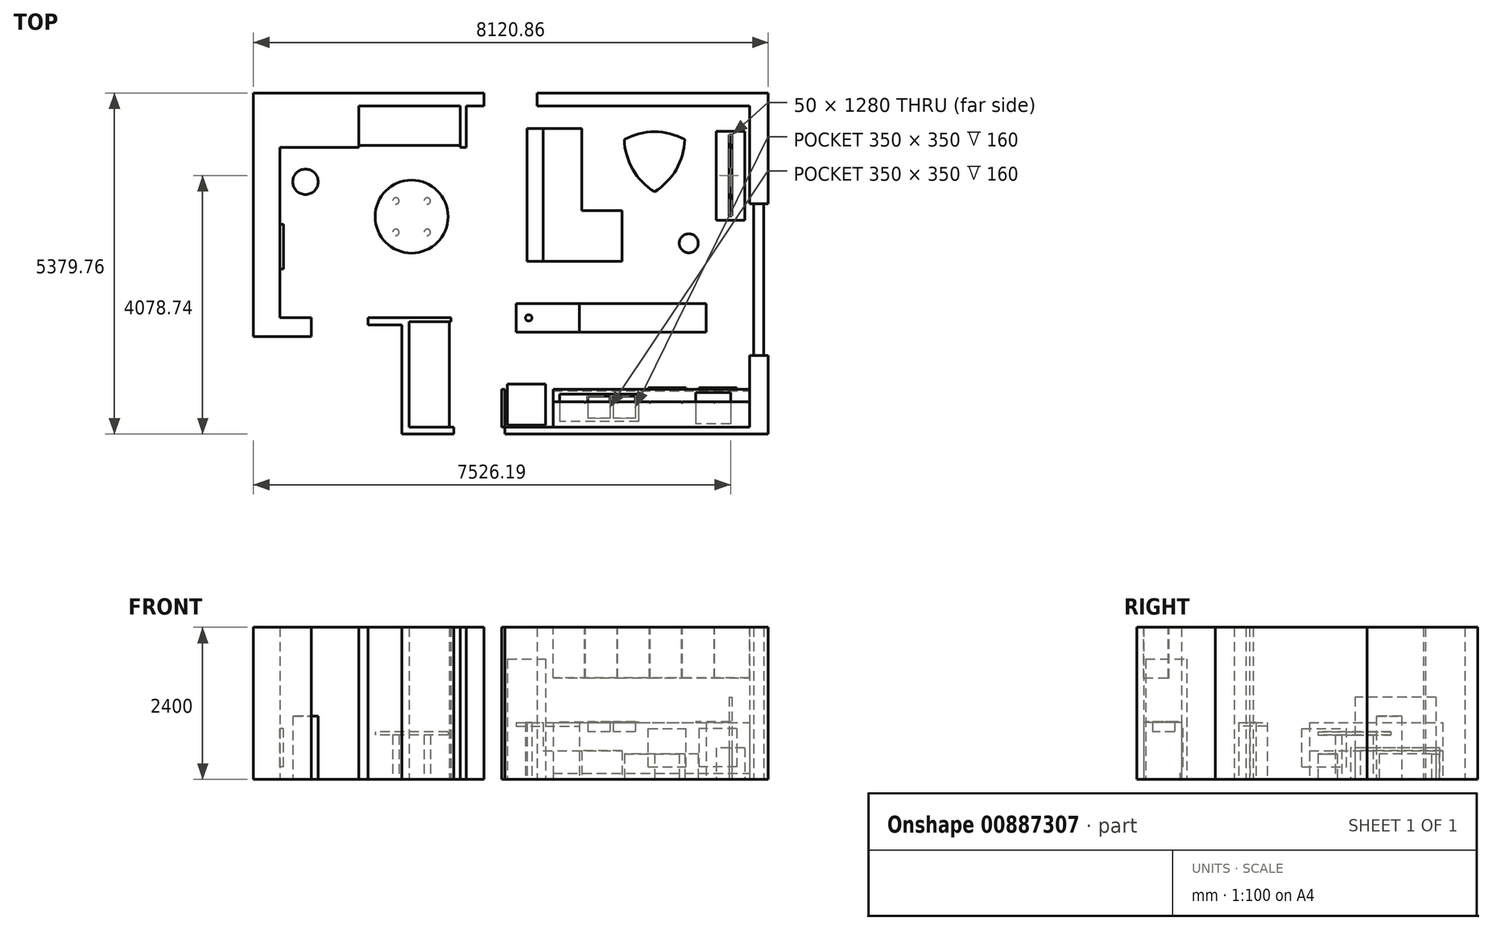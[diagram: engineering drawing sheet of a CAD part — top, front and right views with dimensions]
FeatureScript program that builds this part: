
annotation { "Feature Type Name" : "Feature", "Feature Type Description" : "" }
export const myFeature = defineFeature(function(context is Context, id is Id, definition is map)
    precondition{}
    {
        {
            var Q0;
            Q0=qCreatedBy(makeId("Top.planeOp"),FACE);
            var sketch = newSketch(context, id + "F0", { "sketchPlane" : qUnion([Q0])});
            skLineSegment(sketch, "E0", {"start": v(5332.87, -822.17) * mm, "end": v(1474.75, -822.17) * mm});
            skLineSegment(sketch, "E1", {"start": v(1474.75, -822.17) * mm, "end": v(1474.75, -222.17) * mm});
            skLineSegment(sketch, "E2", {"start": v(1474.75, -222.17) * mm, "end": v(1421.4, -222.17) * mm});
            skLineSegment(sketch, "E3", {"start": v(1421.4, -222.17) * mm, "end": v(1421.4, -822.17) * mm});
            skLineSegment(sketch, "E4", {"start": v(1421.4, -822.17) * mm, "end": v(1474.75, -822.17) * mm});
            skLineSegment(sketch, "E5", {"start": v(5332.87, 309.99) * mm, "end": v(5394.44, 309.99) * mm});
            skLineSegment(sketch, "E6", {"start": v(5394.44, 309.99) * mm, "end": v(5394.44, 2704.75) * mm});
            skLineSegment(sketch, "E7", {"start": v(5394.44, 2704.75) * mm, "end": v(5332.87, 2704.75) * mm});
            skLineSegment(sketch, "E8", {"start": v(5332.87, 2704.75) * mm, "end": v(5332.87, 4243.63) * mm});
            skLineSegment(sketch, "E9", {"start": v(5332.87, 4243.63) * mm, "end": v(1981.19, 4243.63) * mm});
            skLineSegment(sketch, "E10", {"start": v(1981.19, 4243.63) * mm, "end": v(1981.19, 4451) * mm});
            skLineSegment(sketch, "E11", {"start": v(1981.19, 4451) * mm, "end": v(5626.54, 4451) * mm});
            skLineSegment(sketch, "E12", {"start": v(5626.54, 4451) * mm, "end": v(5626.54, 2704.75) * mm});
            skLineSegment(sketch, "E13", {"start": v(5626.54, 2704.75) * mm, "end": v(5394.44, 2704.75) * mm});
            skLineSegment(sketch, "E14", {"start": v(5394.44, 309.99) * mm, "end": v(5626.54, 309.99) * mm});
            skPoint(sketch, "E14.endSnap0", {"position": v(5363.66, 309.99) * mm});
            skLineSegment(sketch, "E15", {"start": v(5626.54, 309.99) * mm, "end": v(5626.54, -928.77) * mm});
            skLineSegment(sketch, "E16", {"start": v(5626.54, -928.77) * mm, "end": v(1474.75, -928.77) * mm});
            skLineSegment(sketch, "E17", {"start": v(1474.75, -928.77) * mm, "end": v(1474.75, -822.17) * mm});
            skLineSegment(sketch, "E18", {"start": v(5558.56, 2704.75) * mm, "end": v(5558.56, 309.99) * mm});
            skLineSegment(sketch, "E19", {"start": v(-37.13, -822.17) * mm, "end": v(664.8, -822.17) * mm});
            skLineSegment(sketch, "E20", {"start": v(664.8, -822.17) * mm, "end": v(664.8, -928.77) * mm});
            skLineSegment(sketch, "E21", {"start": v(664.8, -928.77) * mm, "end": v(-150.57, -928.77) * mm});
            skLineSegment(sketch, "E22", {"start": v(-150.57, -928.77) * mm, "end": v(-150.57, 905.53) * mm});
            skLineSegment(sketch, "E23", {"start": v(-150.57, 905.53) * mm, "end": v(-37.13, 905.53) * mm});
            skLineSegment(sketch, "E24", {"start": v(-37.13, 905.53) * mm, "end": v(-37.13, -26.35) * mm});
            skLineSegment(sketch, "E25", {"start": v(5332.87, 309.99) * mm, "end": v(5332.87, -822.17) * mm});
            skLineSegment(sketch, "E26", {"start": v(-37.13, 905.53) * mm, "end": v(-37.13, -822.17) * mm});
            skLineSegment(sketch, "E27.bottom", {"start": v(1511.94, -792.17) * mm, "end": v(2111.94, -792.17) * mm});
            skLineSegment(sketch, "E27.left", {"start": v(1511.94, -792.17) * mm, "end": v(1511.94, -142.17) * mm});
            skLineSegment(sketch, "E28", {"start": v(1511.94, -142.17) * mm, "end": v(2111.94, -142.17) * mm});
            skLineSegment(sketch, "E29", {"start": v(2111.94, -142.17) * mm, "end": v(2111.94, -792.17) * mm});
            skLineSegment(sketch, "E30", {"start": v(5332.87, -822.17) * mm, "end": v(2232.87, -822.17) * mm, "construction": true});
            skLineSegment(sketch, "E31", {"start": v(2232.87, -822.17) * mm, "end": v(2232.87, -222.17) * mm});
            skLineSegment(sketch, "E32", {"start": v(5332.87, 309.99) * mm, "end": v(4732.87, 309.99) * mm, "construction": true});
            skLineSegment(sketch, "E33", {"start": v(2232.87, -222.17) * mm, "end": v(4732.87, -222.17) * mm});
            skLineSegment(sketch, "E34", {"start": v(4732.87, -222.17) * mm, "end": v(4732.87, 309.99) * mm, "construction": true});
            skLineSegment(sketch, "E35", {"start": v(1647.48, 677.83) * mm, "end": v(4647.48, 677.83) * mm});
            skLineSegment(sketch, "E36", {"start": v(4647.48, 677.83) * mm, "end": v(4647.48, 1127.83) * mm});
            skLineSegment(sketch, "E37", {"start": v(4647.48, 1127.83) * mm, "end": v(1647.48, 1127.83) * mm});
            skLineSegment(sketch, "E38", {"start": v(1647.48, 1127.83) * mm, "end": v(1647.48, 677.83) * mm, "construction": true});
            skLineSegment(sketch, "E39", {"start": v(1822.87, 1793.63) * mm, "end": v(1822.87, 3893.63) * mm});
            skLineSegment(sketch, "E40", {"start": v(1822.87, 3893.63) * mm, "end": v(2682.87, 3893.63) * mm});
            skLineSegment(sketch, "E41", {"start": v(2682.87, 3893.63) * mm, "end": v(2682.87, 2593.63) * mm});
            skLineSegment(sketch, "E42", {"start": v(1822.87, 1793.63) * mm, "end": v(3322.87, 1793.63) * mm});
            skLineSegment(sketch, "E43", {"start": v(3322.87, 1793.63) * mm, "end": v(3322.87, 2593.63) * mm});
            skLineSegment(sketch, "E44", {"start": v(3322.87, 2593.63) * mm, "end": v(2682.87, 2593.63) * mm});
            skLineSegment(sketch, "E45", {"start": v(2072.87, 1793.63) * mm, "end": v(2072.87, 3893.63) * mm});
            skLineSegment(sketch, "E46", {"start": v(2232.87, -549.5) * mm, "end": v(2332.87, -549.5) * mm, "construction": true});
            skLineSegment(sketch, "E47", {"start": v(2332.87, -302.17) * mm, "end": v(2332.87, -732.17) * mm});
            skLineSegment(sketch, "E48", {"start": v(2332.87, -302.17) * mm, "end": v(3582.87, -302.17) * mm});
            skLineSegment(sketch, "E49", {"start": v(3582.87, -302.17) * mm, "end": v(3582.87, -732.17) * mm});
            skLineSegment(sketch, "E50", {"start": v(3582.87, -732.17) * mm, "end": v(2332.87, -732.17) * mm});
            skLineSegment(sketch, "E51", {"start": v(3582.87, -517.17) * mm, "end": v(3532.87, -517.17) * mm, "construction": true});
            skLineSegment(sketch, "E52", {"start": v(3532.87, -517.17) * mm, "end": v(3182.87, -517.17) * mm, "construction": true});
            skLineSegment(sketch, "E53", {"start": v(3182.87, -517.17) * mm, "end": v(3132.87, -517.17) * mm, "construction": true});
            skLineSegment(sketch, "E54", {"start": v(3132.87, -517.17) * mm, "end": v(2782.87, -517.17) * mm, "construction": true});
            skLineSegment(sketch, "E55", {"start": v(3352.05, -302.17) * mm, "end": v(3352.05, -332.17) * mm, "construction": true});
            skLineSegment(sketch, "E56", {"start": v(3352.05, -332.17) * mm, "end": v(3352.05, -682.17) * mm, "construction": true});
            skLineSegment(sketch, "E57.bottom", {"start": v(3532.87, -332.17) * mm, "end": v(3182.87, -332.17) * mm});
            skLineSegment(sketch, "E57.top", {"start": v(3532.87, -682.17) * mm, "end": v(3182.87, -682.17) * mm});
            skLineSegment(sketch, "E57.left", {"start": v(3532.87, -332.17) * mm, "end": v(3532.87, -682.17) * mm});
            skLineSegment(sketch, "E57.right", {"start": v(3182.87, -332.17) * mm, "end": v(3182.87, -682.17) * mm});
            skLineSegment(sketch, "E58.bottom", {"start": v(3132.87, -332.17) * mm, "end": v(2782.87, -332.17) * mm});
            skLineSegment(sketch, "E58.top", {"start": v(3132.87, -682.17) * mm, "end": v(2782.87, -682.17) * mm});
            skLineSegment(sketch, "E58.left", {"start": v(3132.87, -332.17) * mm, "end": v(3132.87, -682.17) * mm});
            skLineSegment(sketch, "E58.right", {"start": v(2782.87, -332.17) * mm, "end": v(2782.87, -682.17) * mm});
            skLineSegment(sketch, "E59.bottom", {"start": v(5032.87, -272.17) * mm, "end": v(4482.87, -272.17) * mm});
            skLineSegment(sketch, "E59.top", {"start": v(5032.87, -772.17) * mm, "end": v(4482.87, -772.17) * mm});
            skLineSegment(sketch, "E59.left", {"start": v(5032.87, -272.17) * mm, "end": v(5032.87, -772.17) * mm});
            skLineSegment(sketch, "E59.right", {"start": v(4482.87, -272.17) * mm, "end": v(4482.87, -772.17) * mm});
            skLineSegment(sketch, "E60", {"start": v(1647.48, 677.83) * mm, "end": v(2647.48, 677.83) * mm, "construction": true});
            skLineSegment(sketch, "E61", {"start": v(2647.48, 677.83) * mm, "end": v(2647.48, 1127.83) * mm});
            skLineSegment(sketch, "E62", {"start": v(2647.48, 902.83) * mm, "end": v(1847.48, 902.83) * mm, "construction": true});
            skCircle(sketch, "E63", {"center": v(1847.48, 902.83) * mm, "radius": 50 * mm});
            skLineSegment(sketch, "E64", {"start": v(5626.54, 309.99) * mm, "end": v(5626.54, -6920.01) * mm, "construction": true});
            skLineSegment(sketch, "E65", {"start": v(5626.54, -6920.01) * mm, "end": v(109096.54, -6920.01) * mm, "construction": true});
            skLineSegment(sketch, "E66", {"start": v(-150.57, 905.53) * mm, "end": v(-687.76, 905.53) * mm});
            skLineSegment(sketch, "E67", {"start": v(-687.76, 905.53) * mm, "end": v(-687.76, 793.16) * mm});
            skLineSegment(sketch, "E68", {"start": v(-687.76, 793.16) * mm, "end": v(-150.57, 793.16) * mm});
            skLineSegment(sketch, "E69", {"start": v(1145.44, 4243.63) * mm, "end": v(-834.24, 4243.63) * mm});
            skLineSegment(sketch, "E70", {"start": v(-834.24, 4243.63) * mm, "end": v(-834.24, 3594.84) * mm});
            skLineSegment(sketch, "E71", {"start": v(-834.24, 3594.84) * mm, "end": v(-2078.37, 3594.84) * mm});
            skLineSegment(sketch, "E72", {"start": v(-2078.37, 3594.84) * mm, "end": v(-2078.37, 905.53) * mm});
            skLineSegment(sketch, "E73", {"start": v(-2078.37, 905.53) * mm, "end": v(-1579.23, 905.53) * mm});
            skLineSegment(sketch, "E74", {"start": v(-1579.23, 905.53) * mm, "end": v(-1579.23, 605.3) * mm});
            skLineSegment(sketch, "E75", {"start": v(-1579.23, 605.3) * mm, "end": v(-2494.32, 605.3) * mm});
            skLineSegment(sketch, "E76", {"start": v(-2494.32, 605.3) * mm, "end": v(-2494.32, 4451) * mm});
            skLineSegment(sketch, "E77", {"start": v(-2494.32, 4451) * mm, "end": v(1145.44, 4451) * mm});
            skLineSegment(sketch, "E78", {"start": v(1145.44, 4451) * mm, "end": v(1145.44, 4243.63) * mm});
            skLineSegment(sketch, "E79", {"start": v(5332.87, 4243.63) * mm, "end": v(5332.87, 4451) * mm});
            skCircle(sketch, "E80", {"center": v(0, 2500.55) * mm, "radius": 350 * mm, "construction": true});
            skLineSegment(sketch, "E81", {"start": v(-247.49, 2748.03) * mm, "end": v(247.49, 2748.03) * mm, "construction": true});
            skLineSegment(sketch, "E82", {"start": v(247.49, 2748.03) * mm, "end": v(247.49, 2253.06) * mm, "construction": true});
            skLineSegment(sketch, "E83", {"start": v(247.49, 2253.06) * mm, "end": v(-247.49, 2253.06) * mm, "construction": true});
            skCircle(sketch, "E84", {"center": v(-247.49, 2748.03) * mm, "radius": 50 * mm});
            skCircle(sketch, "E85", {"center": v(247.49, 2748.03) * mm, "radius": 50 * mm});
            skCircle(sketch, "E86", {"center": v(247.49, 2253.06) * mm, "radius": 50 * mm});
            skCircle(sketch, "E87", {"center": v(-247.49, 2253.06) * mm, "radius": 50 * mm});
            skCircle(sketch, "E88", {"center": v(0, 2500.55) * mm, "radius": 575 * mm});
            skCircle(sketch, "E89", {"center": v(3832.87, 3443.63) * mm, "radius": 550 * mm, "construction": true});
            skLineSegment(sketch, "E90", {"start": v(3832.87, 3443.63) * mm, "end": v(3832.87, 2893.63) * mm, "construction": true});
            skArc(sketch, "E91", {"start": v(3832.87, 2893.63) * mm, "mid": v(4175.58, 3245.77) * mm, "end": v(4309.19, 3718.63) * mm});
            skArc(sketch, "E92", {"start": v(4309.19, 3718.63) * mm, "mid": v(3832.87, 3839.36) * mm, "end": v(3356.56, 3718.63) * mm});
            skArc(sketch, "E93", {"start": v(3356.56, 3718.63) * mm, "mid": v(3490.17, 3245.77) * mm, "end": v(3832.87, 2893.63) * mm});
            skLineSegment(sketch, "E94", {"start": v(3832.87, 3443.63) * mm, "end": v(4309.19, 3718.63) * mm, "construction": true});
            skLineSegment(sketch, "E95", {"start": v(3832.87, 3443.63) * mm, "end": v(3356.56, 3718.63) * mm, "construction": true});
            skLineSegment(sketch, "E96", {"start": v(4309.19, 3718.63) * mm, "end": v(3356.56, 3718.63) * mm, "construction": true});
            skLineSegment(sketch, "E97", {"start": v(3356.56, 3718.63) * mm, "end": v(3832.87, 2893.63) * mm, "construction": true});
            skLineSegment(sketch, "E98", {"start": v(3832.87, 2893.63) * mm, "end": v(4309.19, 3718.63) * mm, "construction": true});
            skCircle(sketch, "E99", {"center": v(4373.05, 2080.44) * mm, "radius": 150 * mm});
            skLineSegment(sketch, "E100", {"start": v(4732.87, -222.17) * mm, "end": v(5332.87, -222.17) * mm});
            skLineSegment(sketch, "E101", {"start": v(865.76, 4243.63) * mm, "end": v(865.76, 3594.84) * mm});
            skLineSegment(sketch, "E102", {"start": v(865.76, 3594.84) * mm, "end": v(765.76, 3594.84) * mm});
            skLineSegment(sketch, "E103", {"start": v(765.76, 3594.84) * mm, "end": v(765.76, 4243.63) * mm});
            skLineSegment(sketch, "E104", {"start": v(765.76, 3627.05) * mm, "end": v(-834.24, 3627.05) * mm});
            skLineSegment(sketch, "E105", {"start": v(597.97, -822.17) * mm, "end": v(597.97, 845.53) * mm});
            skLineSegment(sketch, "E106", {"start": v(597.97, 905.53) * mm, "end": v(624.1, 905.53) * mm});
            skLineSegment(sketch, "E107", {"start": v(624.1, 905.53) * mm, "end": v(624.1, 845.53) * mm});
            skLineSegment(sketch, "E108", {"start": v(624.1, 845.53) * mm, "end": v(-37.13, 845.53) * mm});
            skLineSegment(sketch, "E109", {"start": v(-37.13, 905.53) * mm, "end": v(597.97, 905.53) * mm});
            skCircle(sketch, "E110", {"center": v(-1673.98, 3049.9) * mm, "radius": 200 * mm});
            skLineSegment(sketch, "E111.bottom", {"start": v(5257.71, 3843.63) * mm, "end": v(4807.71, 3843.63) * mm});
            skLineSegment(sketch, "E111.top", {"start": v(5257.71, 2443.63) * mm, "end": v(4807.71, 2443.63) * mm});
            skLineSegment(sketch, "E111.left", {"start": v(5257.71, 3843.63) * mm, "end": v(5257.71, 2443.63) * mm});
            skLineSegment(sketch, "E111.right", {"start": v(4807.71, 3843.63) * mm, "end": v(4807.71, 2443.63) * mm});
            skLineSegment(sketch, "E112.bottom", {"start": v(5006.87, 3789.97) * mm, "end": v(5056.87, 3789.97) * mm});
            skLineSegment(sketch, "E112.top", {"start": v(5006.87, 2509.97) * mm, "end": v(5056.87, 2509.97) * mm});
            skLineSegment(sketch, "E112.left", {"start": v(5006.87, 3789.97) * mm, "end": v(5006.87, 2509.97) * mm});
            skLineSegment(sketch, "E112.right", {"start": v(5056.87, 3789.97) * mm, "end": v(5056.87, 2509.97) * mm});
            skSolve(sketch);
        }
        {
            var Q0;
            {var subQ3=sQuery(id+"F0.wireOp",EDGE,"E7");Q0=makeQuery(id+"F0.imprint","IMPRINT",FACE,{"disambiguationData":[TD([[makeQuery(id+"F0.imprint","IMPRINT",EDGE,{"derivedFrom":subQ3}),-1.0]])]});}
            var Q1;
            {var subQ1=sQuery(id+"F0.wireOp",EDGE,"E5");Q1=makeQuery(id+"F0.imprint","IMPRINT",FACE,{"disambiguationData":[TD([[makeQuery(id+"F0.imprint","IMPRINT",EDGE,{"derivedFrom":subQ1}),-1.0]])]});}
            var Q2;
            {var subQ1=sQuery(id+"F0.wireOp",EDGE,"E20");Q2=makeQuery(id+"F0.imprint","IMPRINT",FACE,{"disambiguationData":[TD([[makeQuery(id+"F0.imprint","IMPRINT",EDGE,{"derivedFrom":subQ1}),-1.0]])]});}
            var Q3;
            Q3=makeQuery(id+"F0.imprint","IMPRINT",FACE,{"disambiguationData":[TD([[makeQuery(id+"F0.imprint","IMPRINT",EDGE,{"derivedFrom":sQuery(id+"F0.wireOp",EDGE,"E1")}),1.0]])]});
            var Q4;
            {var subQ0=sQuery(id+"F0.wireOp",EDGE,"E71");Q4=makeQuery(id+"F0.imprint","IMPRINT",FACE,{"disambiguationData":[TD([[makeQuery(id+"F0.imprint","IMPRINT",EDGE,{"derivedFrom":subQ0}),-1.0]])]});}
            var Q5;
            {var subQ0=sQuery(id+"F0.wireOp",EDGE,"E66");Q5=makeQuery(id+"F0.imprint","IMPRINT",FACE,{"disambiguationData":[TD([[makeQuery(id+"F0.imprint","IMPRINT",EDGE,{"derivedFrom":subQ0}),1.0]])]});}
            var Q6;
            Q6=makeQuery(id+"F0.imprint","IMPRINT",FACE,{"disambiguationData":[TD([[makeQuery(id+"F0.imprint","IMPRINT",EDGE,{"derivedFrom":sQuery(id+"F0.wireOp",EDGE,"E9")}),-1.0]])]});
            var Q7;
            {var subQ5=sQuery(id+"F0.wireOp",EDGE,"E101");Q7=makeQuery(id+"F0.imprint","IMPRINT",FACE,{"disambiguationData":[TD([[makeQuery(id+"F0.imprint","IMPRINT",EDGE,{"derivedFrom":subQ5}),-1.0]])]});}
            var Q8;
            Q8=makeQuery(id+"F0.imprint","IMPRINT",FACE,{"disambiguationData":[TD([[makeQuery(id+"F0.imprint","IMPRINT",EDGE,{"derivedFrom":sQuery(id+"F0.wireOp",EDGE,"E106")}),-1.0]])]});
            extrude(context, id + "F1", {"entities" : qUnion([Q0, Q1, Q2, Q3, Q4, Q5, Q6, Q7, Q8]), "depth" : 2400 * mm, "offsetDistance" : 25 * mm});
        }
        {
            var Q0;
            {var subQ4=sQuery(id+"F0.wireOp",EDGE,"E31");Q0=makeQuery(id+"F0.imprint","IMPRINT",FACE,{"disambiguationData":[TD([[makeQuery(id+"F0.imprint","IMPRINT",EDGE,{"derivedFrom":subQ4}),-1.0]])]});}
            var Q1;
            {var subQ2=sQuery(id+"F0.wireOp",EDGE,"E36");Q1=makeQuery(id+"F0.imprint","IMPRINT",FACE,{"disambiguationData":[TD([[makeQuery(id+"F0.imprint","IMPRINT",EDGE,{"derivedFrom":subQ2}),1.0]])]});}
            var Q2;
            Q2=makeQuery(id+"F0.imprint","IMPRINT",FACE,{"disambiguationData":[TD([[makeQuery(id+"F0.imprint","IMPRINT",EDGE,{"derivedFrom":sQuery(id+"F0.wireOp",EDGE,"E63")}),1.0]])]});
            extrude(context, id + "F2", {"entities" : qUnion([Q0, Q1, Q2]), "depth" : 900 * mm, "offsetDistance" : 25 * mm});
        }
        {
            var Q0;
            Q0=makeQuery(id+"F1.opExtrude","CAP_FACE",FACE,{"disambiguationData":[OSD([sQuery(id+"F0.wireOp",EDGE,"E0"),sQuery(id+"F0.wireOp",EDGE,"E5"),sQuery(id+"F0.wireOp",EDGE,"E14"),sQuery(id+"F0.wireOp",EDGE,"E15"),sQuery(id+"F0.wireOp",EDGE,"E16"),sQuery(id+"F0.wireOp",EDGE,"E17"),sQuery(id+"F0.wireOp",EDGE,"E25")])],"isStart":false});
            var sketch = newSketch(context, id + "F3", { "sketchPlane" : qUnion([Q0])});
            skLineSegment(sketch, "E113", {"start": v(5332.87, -822.17) * mm, "end": v(2232.87, -822.17) * mm});
            skLineSegment(sketch, "E114", {"start": v(2232.87, -822.17) * mm, "end": v(2232.87, -422.17) * mm});
            skLineSegment(sketch, "E115", {"start": v(2232.87, -422.17) * mm, "end": v(5332.87, -422.17) * mm});
            skLineSegment(sketch, "E116", {"start": v(5332.87, -422.17) * mm, "end": v(5332.87, -822.17) * mm});
            skSolve(sketch);
        }
        {
            var Q0;
            Q0=makeQuery(id+"F3.imprint","IMPRINT",FACE,{"disambiguationData":[TD([[makeQuery(id+"F3.imprint","IMPRINT",EDGE,{"derivedFrom":sQuery(id+"F3.wireOp",EDGE,"E113")}),-1.0]])]});
            extrude(context, id + "F4", {"entities" : qUnion([Q0]), "oppositeDirection" : true, "depth" : 800 * mm, "offsetDistance" : 25 * mm});
        }
        {
            var Q0;
            Q0=makeQuery(id+"F0.imprint","IMPRINT",FACE,{"disambiguationData":[TD([[makeQuery(id+"F0.imprint","IMPRINT",EDGE,{"derivedFrom":sQuery(id+"F0.wireOp",EDGE,"E27.bottom")}),1.0]])]});
            extrude(context, id + "F5", {"entities" : qUnion([Q0]), "depth" : 1900 * mm, "offsetDistance" : 25 * mm});
        }
        {
            var Q0;
            {var subQ0=sQuery(id+"F0.wireOp",EDGE,"E39");Q0=makeQuery(id+"F0.imprint","IMPRINT",FACE,{"disambiguationData":[TD([[makeQuery(id+"F0.imprint","IMPRINT",EDGE,{"derivedFrom":subQ0}),-1.0]])]});}
            extrude(context, id + "F6", {"entities" : qUnion([Q0]), "depth" : 900 * mm, "offsetDistance" : 25 * mm});
        }
        {
            var Q0;
            {var subQ3=sQuery(id+"F0.wireOp",EDGE,"E41");Q0=makeQuery(id+"F0.imprint","IMPRINT",FACE,{"disambiguationData":[TD([[makeQuery(id+"F0.imprint","IMPRINT",EDGE,{"derivedFrom":subQ3}),-1.0]])]});}
            extrude(context, id + "F7", {"entities" : qUnion([Q0]), "operationType" : NewBodyOperationType.ADD, "depth" : 450 * mm, "offsetDistance" : 25 * mm});
        }
        {
            var Q0;
            Q0=makeQuery(id+"F0.imprint","IMPRINT",FACE,{"disambiguationData":[TD([[makeQuery(id+"F0.imprint","IMPRINT",EDGE,{"derivedFrom":sQuery(id+"F0.wireOp",EDGE,"E47")}),1.0]])]});
            extrude(context, id + "F8", {"entities" : qUnion([Q0]), "operationType" : NewBodyOperationType.ADD, "depth" : 910 * mm, "offsetDistance" : 25 * mm});
        }
        {
            var Q0;
            Q0=makeQuery(id+"F0.imprint","IMPRINT",FACE,{"disambiguationData":[TD([[makeQuery(id+"F0.imprint","IMPRINT",EDGE,{"derivedFrom":sQuery(id+"F0.wireOp",EDGE,"E57.bottom")}),1.0]])]});
            var Q1;
            Q1=makeQuery(id+"F0.imprint","IMPRINT",FACE,{"disambiguationData":[TD([[makeQuery(id+"F0.imprint","IMPRINT",EDGE,{"derivedFrom":sQuery(id+"F0.wireOp",EDGE,"E58.bottom")}),1.0]])]});
            extrude(context, id + "F9", {"entities" : qUnion([Q0, Q1]), "operationType" : NewBodyOperationType.ADD, "depth" : 750 * mm, "offsetDistance" : 25 * mm});
        }
        {
            var Q0;
            Q0=makeQuery(id+"F0.imprint","IMPRINT",FACE,{"disambiguationData":[TD([[makeQuery(id+"F0.imprint","IMPRINT",EDGE,{"derivedFrom":sQuery(id+"F0.wireOp",EDGE,"E59.bottom")}),1.0]])]});
            extrude(context, id + "F10", {"entities" : qUnion([Q0]), "operationType" : NewBodyOperationType.ADD, "depth" : 910 * mm, "offsetDistance" : 25 * mm});
        }
        {
            var Q0;
            Q0=makeQuery(id+"F2.opExtrude","SWEPT_FACE",FACE,{"disambiguationData":[OSD([sQuery(id+"F0.wireOp",EDGE,"E61")])]});
            var sketch = newSketch(context, id + "F11", { "sketchPlane" : qUnion([Q0])});
            skLineSegment(sketch, "E117.bottom", {"start": v(-1127.83, 900) * mm, "end": v(-527.83, 900) * mm});
            skLineSegment(sketch, "E117.top", {"start": v(-1127.83, 840) * mm, "end": v(-527.83, 840) * mm});
            skLineSegment(sketch, "E117.left", {"start": v(-1127.83, 900) * mm, "end": v(-1127.83, 840) * mm});
            skLineSegment(sketch, "E117.right", {"start": v(-527.83, 900) * mm, "end": v(-527.83, 840) * mm});
            skSolve(sketch);
        }
        {
            var Q0;
            Q0=makeQuery(id+"F11.imprint","IMPRINT",FACE,{"disambiguationData":[TD([[makeQuery(id+"F11.imprint","IMPRINT",EDGE,{"derivedFrom":sQuery(id+"F11.wireOp",EDGE,"E117.bottom")}),1.0]])]});
            extrude(context, id + "F12", {"entities" : qUnion([Q0]), "depth" : 1000 * mm, "offsetDistance" : 25 * mm});
        }
        {
            var Q0;
            {var subQ0=sQuery(id+"F0.wireOp",EDGE,"E6");Q0=makeQuery(id+"F0.imprint","IMPRINT",FACE,{"disambiguationData":[TD([[makeQuery(id+"F0.imprint","IMPRINT",EDGE,{"derivedFrom":subQ0}),-1.0]])]});}
            extrude(context, id + "F13", {"entities" : qUnion([Q0]), "depth" : 2400 * mm, "offsetDistance" : 25 * mm});
        }
        {
            var Q0;
            Q0=makeQuery(id+"F0.imprint","IMPRINT",FACE,{"disambiguationData":[TD([[makeQuery(id+"F0.imprint","IMPRINT",EDGE,{"derivedFrom":sQuery(id+"F0.wireOp",EDGE,"E84")}),-1.0]])]});
            var Q1;
            Q1=makeQuery(id+"Fm7Inrb7nq87sZd_8.opExtrude","CAP_FACE",FACE,{"disambiguationData":[OSD([sQuery(id+"F0.wireOp",EDGE,"E85")])],"isStart":false});
            var Q2;
            Q2=makeQuery(id+"Fm7Inrb7nq87sZd_8.opExtrude","CAP_FACE",FACE,{"disambiguationData":[OSD([sQuery(id+"F0.wireOp",EDGE,"E86")])],"isStart":false});
            var Q3;
            Q3=makeQuery(id+"Fm7Inrb7nq87sZd_8.opExtrude","CAP_FACE",FACE,{"disambiguationData":[OSD([sQuery(id+"F0.wireOp",EDGE,"E84")])],"isStart":false});
            var Q4;
            Q4=makeQuery(id+"Fm7Inrb7nq87sZd_8.opExtrude","CAP_FACE",FACE,{"disambiguationData":[OSD([sQuery(id+"F0.wireOp",EDGE,"E87")])],"isStart":false});
            var Q5;
            Q5=makeQuery(id+"F0.imprint","IMPRINT",FACE,{"disambiguationData":[TD([[makeQuery(id+"F0.imprint","IMPRINT",EDGE,{"derivedFrom":sQuery(id+"F0.wireOp",EDGE,"E85")}),1.0]])]});
            var Q6;
            Q6=makeQuery(id+"F0.imprint","IMPRINT",FACE,{"disambiguationData":[TD([[makeQuery(id+"F0.imprint","IMPRINT",EDGE,{"derivedFrom":sQuery(id+"F0.wireOp",EDGE,"E86")}),1.0]])]});
            var Q7;
            Q7=makeQuery(id+"F0.imprint","IMPRINT",FACE,{"disambiguationData":[TD([[makeQuery(id+"F0.imprint","IMPRINT",EDGE,{"derivedFrom":sQuery(id+"F0.wireOp",EDGE,"E84")}),1.0]])]});
            var Q8;
            Q8=makeQuery(id+"F0.imprint","IMPRINT",FACE,{"disambiguationData":[TD([[makeQuery(id+"F0.imprint","IMPRINT",EDGE,{"derivedFrom":sQuery(id+"F0.wireOp",EDGE,"E87")}),1.0]])]});
            extrude(context, id + "F14", {"entities" : qUnion([Q0, Q1, Q2, Q3, Q4, Q5, Q6, Q7, Q8]), "depth" : 750 * mm, "offsetDistance" : 25 * mm});
        }
        {
            var Q0;
            Q0=makeQuery(id+"F0.imprint","IMPRINT",FACE,{"disambiguationData":[TD([[makeQuery(id+"F0.imprint","IMPRINT",EDGE,{"derivedFrom":sQuery(id+"F0.wireOp",EDGE,"E84")}),-1.0]])]});
            extrude(context, id + "F15", {"entities" : qUnion([Q0]), "depth" : 700 * mm, "offsetDistance" : 25 * mm});
        }
        {
            var Q0;
            Q0=makeQuery(id+"F15.opExtrude","SWEPT_BODY",BODY,{"disambiguationData":[OSD([sQuery(id+"F0.wireOp",EDGE,"E84"),sQuery(id+"F0.wireOp",EDGE,"E85"),sQuery(id+"F0.wireOp",EDGE,"E86"),sQuery(id+"F0.wireOp",EDGE,"E87"),sQuery(id+"F0.wireOp",EDGE,"E88")])]});
            var Q1;
            Q1=makeQuery(id+"F14.opExtrude","SWEPT_BODY",BODY,{"disambiguationData":[OSD([sQuery(id+"F0.wireOp",EDGE,"E88")])]});
            booleanBodies(context, id + "F16", {"operationType" : BooleanOperationType.SUBTRACTION, "tools" : qUnion([Q0]), "targets" : qUnion([Q1])});
        }
        {
            var Q0;
            Q0=makeQuery(id+"F0.imprint","IMPRINT",FACE,{"disambiguationData":[TD([[makeQuery(id+"F0.imprint","IMPRINT",EDGE,{"derivedFrom":sQuery(id+"F0.wireOp",EDGE,"E91")}),1.0]])]});
            var Q1;
            Q1=makeQuery(id+"F0.imprint","IMPRINT",FACE,{"disambiguationData":[TD([[makeQuery(id+"F0.imprint","IMPRINT",EDGE,{"derivedFrom":sQuery(id+"F0.wireOp",EDGE,"ivdHgasm-OcnA-kCRU-FAQQ-BUchxxMC1X0W")}),1.0]])]});
            var Q2;
            Q2=makeQuery(id+"F0.imprint","IMPRINT",FACE,{"disambiguationData":[TD([[makeQuery(id+"F0.imprint","IMPRINT",EDGE,{"derivedFrom":sQuery(id+"F0.wireOp",EDGE,"E99")}),1.0]])]});
            extrude(context, id + "F17", {"entities" : qUnion([Q0, Q1, Q2]), "depth" : 400 * mm, "offsetDistance" : 25 * mm});
        }
        {
            var Q0;
            Q0=makeQuery(id+"F2.opExtrude","SWEPT_FACE",FACE,{"disambiguationData":[OSD([sQuery(id+"F0.wireOp",EDGE,"E33"),sQuery(id+"F0.wireOp",EDGE,"E100")])]});
            var sketch = newSketch(context, id + "F18", { "sketchPlane" : qUnion([Q0])});
            skLineSegment(sketch, "E118", {"start": v(-2232.87, 100) * mm, "end": v(-2232.87, 100) * mm});
            skLineSegment(sketch, "E119.bottom", {"start": v(-3732.87, 200) * mm, "end": v(-4332.87, 200) * mm});
            skLineSegment(sketch, "E119.top", {"start": v(-3732.87, 800) * mm, "end": v(-4332.87, 800) * mm});
            skLineSegment(sketch, "E119.left", {"start": v(-3732.87, 200) * mm, "end": v(-3732.87, 800) * mm});
            skLineSegment(sketch, "E119.right", {"start": v(-4332.87, 200) * mm, "end": v(-4332.87, 800) * mm});
            skLineSegment(sketch, "E120", {"start": v(-2232.87, 900) * mm, "end": v(-2232.87, 0) * mm, "construction": true});
            skLineSegment(sketch, "E121.bottom", {"start": v(-5132.87, 800) * mm, "end": v(-4532.87, 800) * mm});
            skLineSegment(sketch, "E121.top", {"start": v(-5132.87, 200) * mm, "end": v(-4532.87, 200) * mm});
            skLineSegment(sketch, "E121.left", {"start": v(-5132.87, 800) * mm, "end": v(-5132.87, 200) * mm});
            skLineSegment(sketch, "E121.right", {"start": v(-4532.87, 800) * mm, "end": v(-4532.87, 200) * mm});
            skLineSegment(sketch, "E122", {"start": v(-2232.87, 100) * mm, "end": v(-5332.87, 100) * mm});
            skSolve(sketch);
        }
        {
            var Q0;
            Q0=makeQuery(id+"F18.imprint","IMPRINT",FACE,{"disambiguationData":[TD([[makeQuery(id+"F18.imprint","IMPRINT",EDGE,{"derivedFrom":sQuery(id+"F18.wireOp",EDGE,"E121.bottom")}),-1.0]])]});
            var Q1;
            Q1=makeQuery(id+"F18.imprint","IMPRINT",FACE,{"disambiguationData":[TD([[makeQuery(id+"F18.imprint","IMPRINT",EDGE,{"derivedFrom":sQuery(id+"F18.wireOp",EDGE,"E119.bottom")}),-1.0]])]});
            extrude(context, id + "F19", {"entities" : qUnion([Q0, Q1]), "operationType" : NewBodyOperationType.ADD, "depth" : 25 * mm, "offsetDistance" : 25 * mm});
        }
        {
            var Q0;
            {var subQ0=sQuery(id+"F18.wireOp",EDGE,"E122");Q0=makeQuery(id+"F18.imprint","IMPRINT",FACE,{"disambiguationData":[TD([[makeQuery(id+"F18.imprint","IMPRINT",EDGE,{"derivedFrom":subQ0}),1.0]])]});}
            extrude(context, id + "F20", {"entities" : qUnion([Q0]), "operationType" : NewBodyOperationType.REMOVE, "oppositeDirection" : true, "depth" : 30 * mm, "offsetDistance" : 25 * mm});
        }
        {
            var Q0;
            Q0=makeQuery(id+"F4.opExtrude","SWEPT_FACE",FACE,{"disambiguationData":[OSD([sQuery(id+"F3.wireOp",EDGE,"E115")])]});
            var sketch = newSketch(context, id + "F21", { "sketchPlane" : qUnion([Q0])});
            skLineSegment(sketch, "E123", {"start": v(-5332.87, 1600) * mm, "end": v(-5332.87, 2400) * mm, "construction": true});
            skLineSegment(sketch, "E124", {"start": v(-2232.87, 1600) * mm, "end": v(-2732.87, 1600) * mm, "construction": true});
            skLineSegment(sketch, "E125.bottom", {"start": v(-2732.87, 1600) * mm, "end": v(-2742.87, 1600) * mm});
            skLineSegment(sketch, "E125.top", {"start": v(-2732.87, 2400) * mm, "end": v(-2742.87, 2400) * mm});
            skLineSegment(sketch, "E125.left", {"start": v(-2732.87, 1600) * mm, "end": v(-2732.87, 2400) * mm});
            skLineSegment(sketch, "E125.right", {"start": v(-2742.87, 1600) * mm, "end": v(-2742.87, 2400) * mm});
            skLineSegment(sketch, "E126", {"start": v(-2742.87, 1600) * mm, "end": v(-3242.87, 1600) * mm, "construction": true});
            skLineSegment(sketch, "E127", {"start": v(-3242.87, 1600) * mm, "end": v(-3752.87, 1600) * mm, "construction": true});
            skLineSegment(sketch, "E128", {"start": v(-3752.87, 1600) * mm, "end": v(-4262.87, 1600) * mm, "construction": true});
            skLineSegment(sketch, "E129", {"start": v(-4262.87, 1600) * mm, "end": v(-4772.87, 1600) * mm, "construction": true});
            skLineSegment(sketch, "E130.bottom", {"start": v(-3242.87, 1600) * mm, "end": v(-3252.87, 1600) * mm});
            skLineSegment(sketch, "E130.top", {"start": v(-3242.87, 2400) * mm, "end": v(-3252.87, 2400) * mm});
            skLineSegment(sketch, "E130.left", {"start": v(-3242.87, 1600) * mm, "end": v(-3242.87, 2400) * mm});
            skLineSegment(sketch, "E130.right", {"start": v(-3252.87, 1600) * mm, "end": v(-3252.87, 2400) * mm});
            skLineSegment(sketch, "E131.bottom", {"start": v(-3752.87, 1600) * mm, "end": v(-3762.87, 1600) * mm});
            skLineSegment(sketch, "E131.top", {"start": v(-3752.87, 2400) * mm, "end": v(-3762.87, 2400) * mm});
            skLineSegment(sketch, "E131.left", {"start": v(-3752.87, 1600) * mm, "end": v(-3752.87, 2400) * mm});
            skLineSegment(sketch, "E131.right", {"start": v(-3762.87, 1600) * mm, "end": v(-3762.87, 2400) * mm});
            skLineSegment(sketch, "E132.bottom", {"start": v(-4262.87, 1600) * mm, "end": v(-4272.87, 1600) * mm});
            skLineSegment(sketch, "E132.top", {"start": v(-4262.87, 2400) * mm, "end": v(-4272.87, 2400) * mm});
            skLineSegment(sketch, "E132.left", {"start": v(-4262.87, 1600) * mm, "end": v(-4262.87, 2400) * mm});
            skLineSegment(sketch, "E132.right", {"start": v(-4272.87, 1600) * mm, "end": v(-4272.87, 2400) * mm});
            skLineSegment(sketch, "E133.bottom", {"start": v(-4772.87, 1600) * mm, "end": v(-4782.87, 1600) * mm});
            skLineSegment(sketch, "E133.top", {"start": v(-4772.87, 2400) * mm, "end": v(-4782.87, 2400) * mm});
            skLineSegment(sketch, "E133.left", {"start": v(-4772.87, 1600) * mm, "end": v(-4772.87, 2400) * mm});
            skLineSegment(sketch, "E133.right", {"start": v(-4782.87, 1600) * mm, "end": v(-4782.87, 2400) * mm});
            skLineSegment(sketch, "E134", {"start": v(-4782.87, 1600) * mm, "end": v(-5282.87, 1600) * mm, "construction": true});
            skSolve(sketch);
        }
        {
            var Q0;
            Q0=makeQuery(id+"F21.imprint","IMPRINT",FACE,{"disambiguationData":[TD([[makeQuery(id+"F21.imprint","IMPRINT",EDGE,{"derivedFrom":sQuery(id+"F21.wireOp",EDGE,"E125.bottom")}),-1.0]])]});
            var Q1;
            Q1=makeQuery(id+"F21.imprint","IMPRINT",FACE,{"disambiguationData":[TD([[makeQuery(id+"F21.imprint","IMPRINT",EDGE,{"derivedFrom":sQuery(id+"F21.wireOp",EDGE,"E130.bottom")}),-1.0]])]});
            var Q2;
            Q2=makeQuery(id+"F21.imprint","IMPRINT",FACE,{"disambiguationData":[TD([[makeQuery(id+"F21.imprint","IMPRINT",EDGE,{"derivedFrom":sQuery(id+"F21.wireOp",EDGE,"E131.bottom")}),-1.0]])]});
            var Q3;
            Q3=makeQuery(id+"F21.imprint","IMPRINT",FACE,{"disambiguationData":[TD([[makeQuery(id+"F21.imprint","IMPRINT",EDGE,{"derivedFrom":sQuery(id+"F21.wireOp",EDGE,"E132.bottom")}),-1.0]])]});
            var Q4;
            Q4=makeQuery(id+"F21.imprint","IMPRINT",FACE,{"disambiguationData":[TD([[makeQuery(id+"F21.imprint","IMPRINT",EDGE,{"derivedFrom":sQuery(id+"F21.wireOp",EDGE,"E133.bottom")}),-1.0]])]});
            extrude(context, id + "F22", {"entities" : qUnion([Q0, Q1, Q2, Q3, Q4]), "operationType" : NewBodyOperationType.REMOVE, "oppositeDirection" : true, "depth" : 10 * mm, "offsetDistance" : 25 * mm});
        }
        {
            var Q0;
            Q0=makeQuery(id+"F1.opExtrude","SWEPT_FACE",FACE,{"disambiguationData":[OSD([sQuery(id+"F0.wireOp",EDGE,"E72")])]});
            var sketch = newSketch(context, id + "F23", { "sketchPlane" : qUnion([Q0])});
            skLineSegment(sketch, "E135.bottom", {"start": v(1676.7, 200) * mm, "end": v(2376.7, 200) * mm});
            skLineSegment(sketch, "E135.top", {"start": v(1676.7, 800) * mm, "end": v(2376.7, 800) * mm});
            skLineSegment(sketch, "E135.left", {"start": v(1676.7, 200) * mm, "end": v(1676.7, 800) * mm});
            skLineSegment(sketch, "E135.right", {"start": v(2376.7, 200) * mm, "end": v(2376.7, 800) * mm});
            skSolve(sketch);
        }
        {
            var Q0;
            Q0=makeQuery(id+"F23.imprint","IMPRINT",FACE,{"disambiguationData":[TD([[makeQuery(id+"F23.imprint","IMPRINT",EDGE,{"derivedFrom":sQuery(id+"F23.wireOp",EDGE,"E135.bottom")}),1.0]])]});
            extrude(context, id + "F24", {"entities" : qUnion([Q0]), "depth" : 60 * mm, "offsetDistance" : 25 * mm});
        }
        {
            var Q0;
            {var subQ5=sQuery(id+"F0.wireOp",EDGE,"E104");Q0=makeQuery(id+"F0.imprint","IMPRINT",FACE,{"disambiguationData":[TD([[makeQuery(id+"F0.imprint","IMPRINT",EDGE,{"derivedFrom":subQ5}),-1.0]])]});}
            var Q1;
            {var subQ0=sQuery(id+"F0.wireOp",EDGE,"E26");Q1=makeQuery(id+"F0.imprint","IMPRINT",FACE,{"disambiguationData":[TD([[makeQuery(id+"F0.imprint","IMPRINT",EDGE,{"derivedFrom":subQ0}),1.0]])]});}
            extrude(context, id + "F25", {"entities" : qUnion([Q0, Q1]), "depth" : 2400 * mm, "offsetDistance" : 25 * mm});
        }
        {
            var Q0;
            Q0=makeQuery(id+"F0.imprint","IMPRINT",FACE,{"disambiguationData":[TD([[makeQuery(id+"F0.imprint","IMPRINT",EDGE,{"derivedFrom":sQuery(id+"F0.wireOp",EDGE,"E110")}),1.0]])]});
            extrude(context, id + "F26", {"entities" : qUnion([Q0]), "depth" : 1000 * mm, "offsetDistance" : 25 * mm});
        }
        {
            var Q0;
            Q0=makeQuery(id+"F0.imprint","IMPRINT",FACE,{"disambiguationData":[TD([[makeQuery(id+"F0.imprint","IMPRINT",EDGE,{"derivedFrom":sQuery(id+"F0.wireOp",EDGE,"E111.bottom")}),1.0]])]});
            extrude(context, id + "F27", {"entities" : qUnion([Q0]), "depth" : 500 * mm, "offsetDistance" : 25 * mm});
        }
        {
            var Q0;
            Q0=makeQuery(id+"F0.imprint","IMPRINT",FACE,{"disambiguationData":[TD([[makeQuery(id+"F0.imprint","IMPRINT",EDGE,{"derivedFrom":sQuery(id+"F0.wireOp",EDGE,"E112.bottom")}),-1.0]])]});
            extrude(context, id + "F28", {"entities" : qUnion([Q0]), "depth" : 1300 * mm, "offsetDistance" : 25 * mm});
        }
    });
